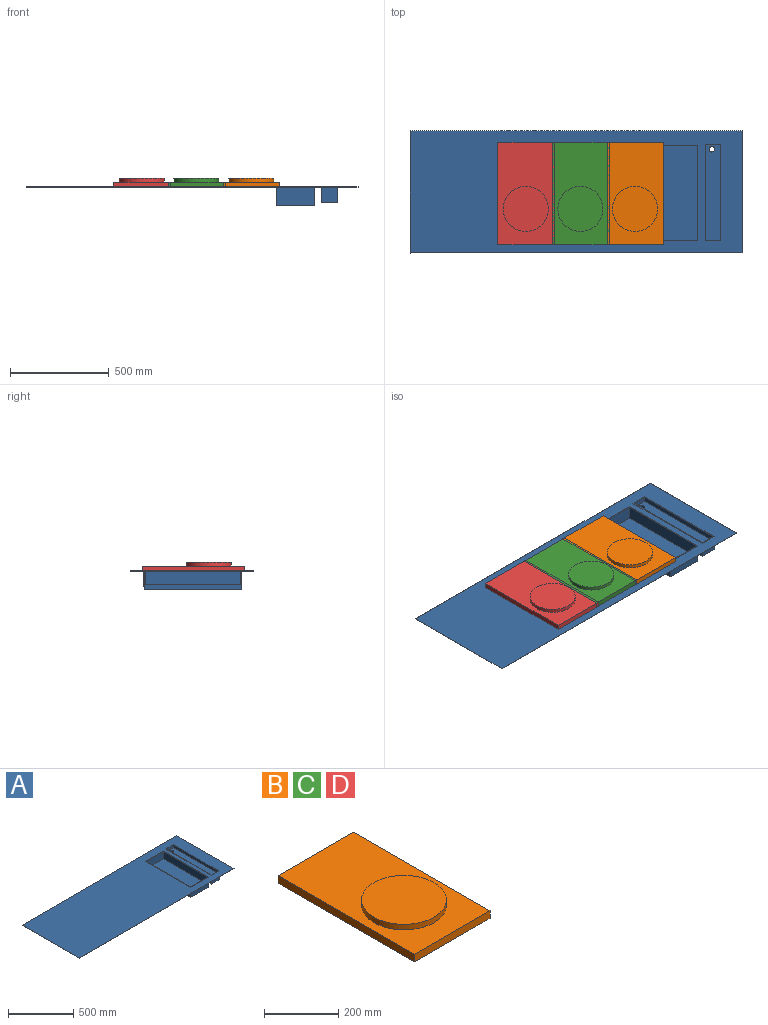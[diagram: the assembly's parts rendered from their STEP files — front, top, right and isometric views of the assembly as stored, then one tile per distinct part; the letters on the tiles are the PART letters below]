
ASSEMBLY  parts=4 mates=3
PART A: 29 faces, bbox 1683x621x94 mm
  f0: plane 1683x621mm, normal (0,0,1), area 915099.1mm2, adj f3,f4,f5,f6,f7,f8,f14,f15
  f1: cylinder r=14.13mm len=56mm, axis (0,0,1), area 4973.1mm2, adj f23,f24
  f2: plane 1683x621mm, normal (0,0,-1), area 903737.1mm2, adj f3,f4,f5,f6,f7,f8,f9,f10
  f3: plane 2x1mm, normal (1,0,0), area 2mm2, adj f0,f2,f4,f8
  f4: plane 1681x1mm, normal (0,-1,0), area 1681mm2, adj f0,f2,f3,f5
  f5: plane 619x1mm, normal (1,0,0), area 619mm2, adj f0,f2,f4,f6
  f6: plane 1683x1mm, normal (0,1,0), area 1683mm2, adj f0,f2,f5,f7
  f7: plane 621x1mm, normal (-1,0,0), area 621mm2, adj f0,f2,f6,f8
  f8: plane 2x1mm, normal (0,-1,0), area 2mm2, adj f0,f2,f3,f7
  f9: plane 195.56x93mm, normal (0,1,0), area 18187.2mm2, adj f2,f10,f12,f13
  f10: plane 491.84x93mm, normal (-1,0,0), area 45741.2mm2, adj f2,f9,f11,f13
  f11: plane 195.56x93mm, normal (0,-1,0), area 18187.2mm2, adj f2,f10,f12,f13
  f12: plane 491.84x93mm, normal (1,0,0), area 45741.2mm2, adj f2,f9,f11,f13
  f13: plane 491.84x195.56mm, normal (0,0,-1), area 96184.8mm2, adj f9,f10,f11,f12
  f14: plane 481.84x68mm, normal (-1,0,0), area 32765.2mm2, adj f0,f15,f17,f18
  f15: plane 185.56x68mm, normal (0,-1,0), area 12618.1mm2, adj f0,f14,f16,f18
  f16: plane 481.84x68mm, normal (1,0,0), area 32765.2mm2, adj f0,f15,f17,f18
  f17: plane 185.56x68mm, normal (0,1,0), area 12618.1mm2, adj f0,f14,f16,f18
  f18: plane 481.84x185.56mm, normal (0,0,1), area 89410.8mm2, adj f14,f15,f16,f17
  f19: plane 497.35x80mm, normal (-1,0,0), area 39787.9mm2, adj f2,f20,f22,f23
  f20: plane 84.16x80mm, normal (0,-1,0), area 6733.2mm2, adj f2,f19,f21,f23
  f21: plane 497.35x80mm, normal (1,0,0), area 39787.9mm2, adj f2,f20,f22,f23
  f22: plane 84.16x80mm, normal (0,1,0), area 6733.2mm2, adj f2,f19,f21,f23
  f23: plane 497.35x84.16mm, normal (0,0,-1), area 41231.5mm2, adj f1,f19,f20,f21,f22
  f24: plane 489.35x76.16mm, normal (0,0,1), area 36643.5mm2, adj f1,f25,f26,f27,f28
  f25: plane 76.16x25mm, normal (0,-1,0), area 1904.1mm2, adj f0,f24,f26,f28
  f26: plane 489.35x25mm, normal (1,0,0), area 12233.7mm2, adj f0,f24,f25,f27
  f27: plane 76.16x25mm, normal (0,1,0), area 1904.1mm2, adj f0,f24,f26,f28
  f28: plane 489.35x25mm, normal (-1,0,0), area 12233.7mm2, adj f0,f24,f25,f27
PART B: 8 faces, bbox 288x520x43 mm
  f0: plane 288x25mm, normal (0,1,0), area 7200mm2, adj f1,f3,f4,f5
  f1: plane 520x25mm, normal (-1,0,0), area 13000mm2, adj f0,f2,f4,f5
  f2: plane 288x25mm, normal (0,-1,0), area 7200mm2, adj f1,f3,f4,f5
  f3: plane 520x25mm, normal (1,0,0), area 13000mm2, adj f0,f2,f4,f5
  f4: plane 520x288mm, normal (0,0,1), area 108713.3mm2, adj f0,f1,f2,f3,f6
  f5: plane 520x288mm, normal (0,0,-1), area 149760mm2, adj f0,f1,f2,f3
  f6: cylinder r=114.3mm len=228.61mm, axis (0,0,-1), area 12927.6mm2, adj f4,f7
  f7: plane 228.61x228.61mm, normal (0,0,1), area 41046.7mm2, adj f6
PART C: same geometry as B
PART D: same geometry as B
PLACE A at identity fixed
PLACE B t=(666.3,-11.45,0)mm
PLACE C t=(389.3,-11.45,0)mm
PLACE D t=(112.3,-11.45,0)mm
MATE fastened C.f5 <-> A.f0  axis (0,0,1) through (722.02,42.72,0)mm
MATE fastened B.f5 <-> A.f0  axis (0,0,1) through (999.02,42.72,0)mm
MATE fastened D.f5 <-> A.f0  axis (0,0,1) through (445.02,42.72,0)mm
